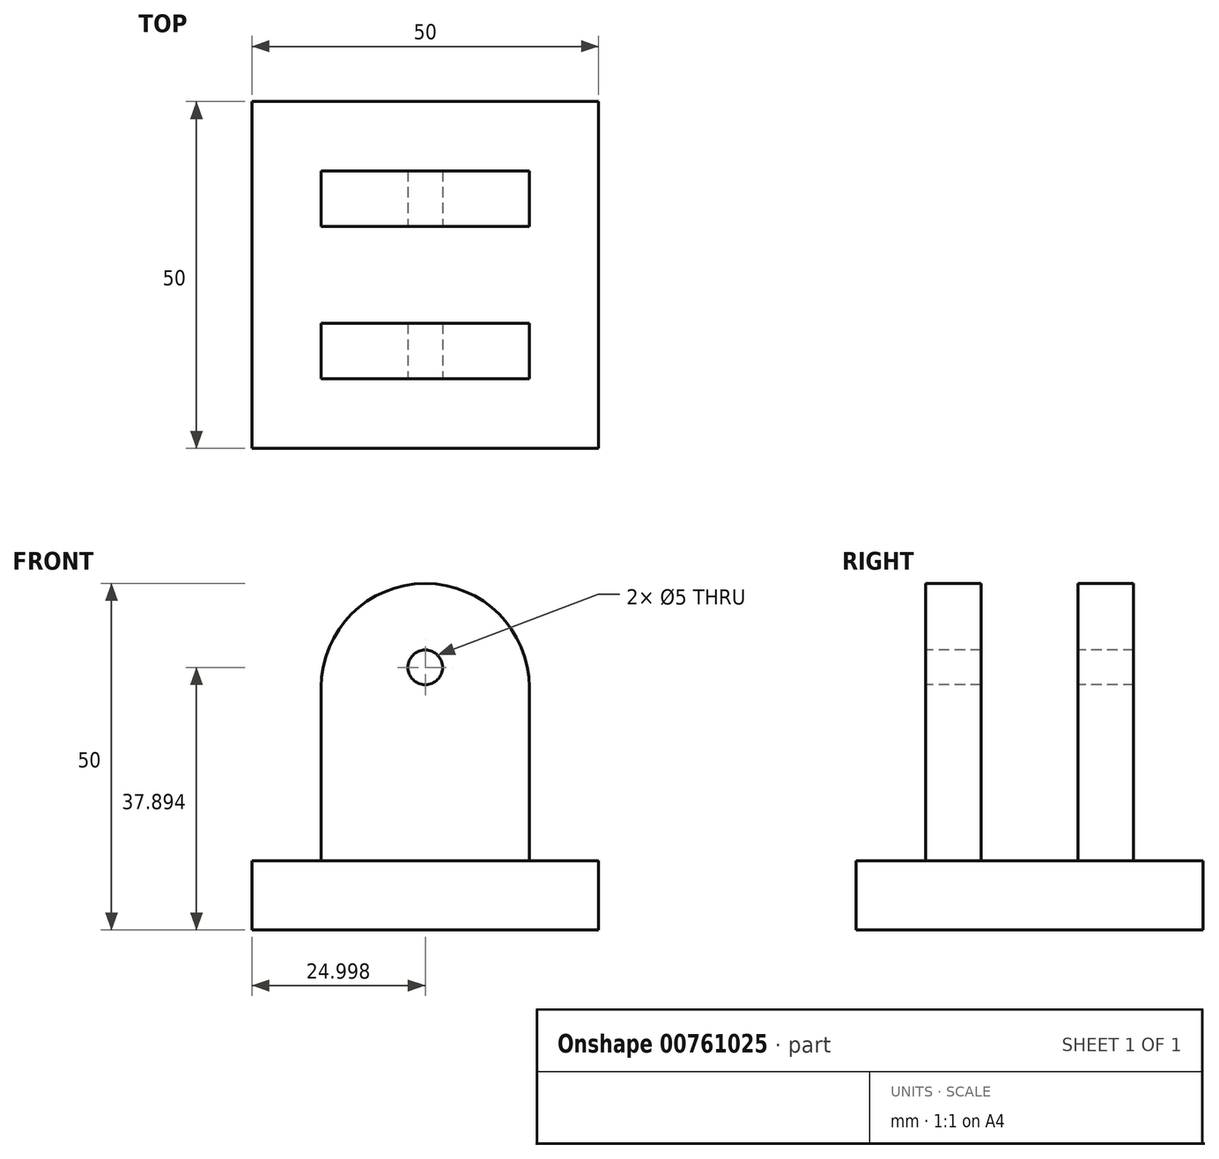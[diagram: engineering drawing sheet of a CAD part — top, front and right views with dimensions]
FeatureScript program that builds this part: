
annotation { "Feature Type Name" : "Feature", "Feature Type Description" : "" }
export const myFeature = defineFeature(function(context is Context, id is Id, definition is map)
    precondition{}
    {
        {
            var Q0;
            Q0=qCreatedBy(makeId("Top.planeOp"),FACE);
            var sketch = newSketch(context, id + "F0", { "sketchPlane" : qUnion([Q0])});
            skLineSegment(sketch, "E0.bottom", {"start": v(-23.83, 27.47) * mm, "end": v(26.17, 27.47) * mm});
            skLineSegment(sketch, "E0.top", {"start": v(-23.83, -22.53) * mm, "end": v(26.17, -22.53) * mm});
            skLineSegment(sketch, "E0.left", {"start": v(-23.83, 27.47) * mm, "end": v(-23.83, -22.53) * mm});
            skLineSegment(sketch, "E0.right", {"start": v(26.17, 27.47) * mm, "end": v(26.17, -22.53) * mm});
            skSolve(sketch);
        }
        {
            var Q0;
            Q0=makeQuery(id+"F0.imprint","IMPRINT",FACE,{"disambiguationData":[TD([[makeQuery(id+"F0.imprint","IMPRINT",EDGE,{"derivedFrom":sQuery(id+"F0.wireOp",EDGE,"E0.bottom")}),-1.0]])]});
            extrude(context, id + "F1", {"entities" : qUnion([Q0]), "depth" : 10 * mm, "offsetDistance" : 25 * mm});
        }
        {
            var Q0;
            Q0=makeQuery(id+"F1.opExtrude","CAP_FACE",FACE,{"disambiguationData":[OSD([sQuery(id+"F0.wireOp",EDGE,"E0.bottom"),sQuery(id+"F0.wireOp",EDGE,"E0.top"),sQuery(id+"F0.wireOp",EDGE,"E0.left"),sQuery(id+"F0.wireOp",EDGE,"E0.right")])],"isStart":false});
            var sketch = newSketch(context, id + "F2", { "sketchPlane" : qUnion([Q0])});
            skLineSegment(sketch, "E1.bottom", {"start": v(-13.83, 17.47) * mm, "end": v(16.17, 17.47) * mm});
            skLineSegment(sketch, "E1.top", {"start": v(-13.83, 9.47) * mm, "end": v(16.17, 9.47) * mm});
            skLineSegment(sketch, "E1.left", {"start": v(-13.83, 17.47) * mm, "end": v(-13.83, 9.47) * mm});
            skLineSegment(sketch, "E1.right", {"start": v(16.17, 17.47) * mm, "end": v(16.17, 9.47) * mm});
            skLineSegment(sketch, "E2.bottom", {"start": v(-13.83, -4.53) * mm, "end": v(16.17, -4.53) * mm});
            skLineSegment(sketch, "E2.top", {"start": v(-13.83, -12.53) * mm, "end": v(16.17, -12.53) * mm});
            skLineSegment(sketch, "E2.left", {"start": v(-13.83, -4.53) * mm, "end": v(-13.83, -12.53) * mm});
            skLineSegment(sketch, "E2.right", {"start": v(16.17, -4.53) * mm, "end": v(16.17, -12.53) * mm});
            skSolve(sketch);
        }
        {
            var Q0;
            Q0=makeQuery(id+"F2.imprint","IMPRINT",FACE,{"disambiguationData":[TD([[makeQuery(id+"F2.imprint","IMPRINT",EDGE,{"derivedFrom":sQuery(id+"F2.wireOp",EDGE,"E2.bottom")}),-1.0]])]});
            extrude(context, id + "F3", {"entities" : qUnion([Q0]), "operationType" : NewBodyOperationType.ADD, "depth" : 40 * mm, "offsetDistance" : 25 * mm});
        }
        {
            var Q0;
            Q0=makeQuery(id+"F1.opExtrude","CAP_FACE",FACE,{"disambiguationData":[OSD([sQuery(id+"F0.wireOp",EDGE,"E0.bottom"),sQuery(id+"F0.wireOp",EDGE,"E0.top"),sQuery(id+"F0.wireOp",EDGE,"E0.left"),sQuery(id+"F0.wireOp",EDGE,"E0.right")])],"isStart":false});
            var sketch = newSketch(context, id + "F4", { "sketchPlane" : qUnion([Q0])});
            skLineSegment(sketch, "E3.bottom", {"start": v(-13.83, 17.47) * mm, "end": v(16.17, 17.47) * mm});
            skLineSegment(sketch, "E3.top", {"start": v(-13.83, 9.47) * mm, "end": v(16.17, 9.47) * mm});
            skLineSegment(sketch, "E3.left", {"start": v(-13.83, 17.47) * mm, "end": v(-13.83, 9.47) * mm});
            skLineSegment(sketch, "E3.right", {"start": v(16.17, 17.47) * mm, "end": v(16.17, 9.47) * mm});
            skSolve(sketch);
        }
        {
            var Q0;
            Q0=makeQuery(id+"F4.imprint","IMPRINT",FACE,{"disambiguationData":[TD([[makeQuery(id+"F4.imprint","IMPRINT",EDGE,{"derivedFrom":sQuery(id+"F4.wireOp",EDGE,"E3.bottom")}),-1.0]])]});
            extrude(context, id + "F5", {"entities" : qUnion([Q0]), "operationType" : NewBodyOperationType.ADD, "depth" : 40 * mm, "offsetDistance" : 25 * mm});
        }
        {
            var Q0;
            Q0=makeQuery(id+"F3.opExtrude","CAP_EDGE",EDGE,{"disambiguationData":[OSD([sQuery(id+"F2.wireOp",EDGE,"E2.left")])],"isStart":false});
            var Q1;
            Q1=makeQuery(id+"F3.opExtrude","CAP_EDGE",EDGE,{"disambiguationData":[OSD([sQuery(id+"F2.wireOp",EDGE,"E2.right")])],"isStart":false});
            fillet(context, id + "F6", {"entities" : qUnion([Q0, Q1]), "radius" : 15 * mm, "tangentPropagation" : true, "allowEdgeOverflow" : false});
        }
        {
            var Q0;
            Q0=makeQuery(id+"F5.opExtrude","CAP_EDGE",EDGE,{"disambiguationData":[OSD([sQuery(id+"F4.wireOp",EDGE,"E3.right")])],"isStart":false});
            var Q1;
            Q1=makeQuery(id+"F5.opExtrude","CAP_EDGE",EDGE,{"disambiguationData":[OSD([sQuery(id+"F4.wireOp",EDGE,"E3.left")])],"isStart":false});
            fillet(context, id + "F7", {"entities" : qUnion([Q0, Q1]), "radius" : 15 * mm, "tangentPropagation" : true, "allowEdgeOverflow" : false});
        }
        {
            var Q0;
            Q0=makeQuery(id+"F3.opExtrude","SWEPT_FACE",FACE,{"disambiguationData":[OSD([sQuery(id+"F2.wireOp",EDGE,"E2.top")])]});
            var sketch = newSketch(context, id + "F8", { "sketchPlane" : qUnion([Q0])});
            skPoint(sketch, "E4", {"position": v(1.17, 37.9) * mm});
            skPoint(sketch, "E4.positionSnap0", {"position": v(1.17, 50) * mm});
            skSolve(sketch);
        }
        {
            var Q0;
            Q0=sQuery(id+"F8.wireOp",VERTEX,"E4");
            var Q1;
            Q1=makeQuery(id+"F1.opExtrude","SWEPT_BODY",BODY,{"disambiguationData":[OSD([sQuery(id+"F0.wireOp",EDGE,"E0.bottom"),sQuery(id+"F0.wireOp",EDGE,"E0.top"),sQuery(id+"F0.wireOp",EDGE,"E0.left"),sQuery(id+"F0.wireOp",EDGE,"E0.right")])]});
            hole(context, id + "F9", {"style" : HoleStyle.SIMPLE, "endStyle" : HoleEndStyle.THROUGH, "holeDiameter" : 5 * mm, "majorDiameter" : 5 * mm, "isTappedThrough" : true, "tappedDepth" : 12 * mm, "tapClearance" : 3, "locations" : qUnion([Q0]), "scope" : qUnion([Q1])});
        }
    });
